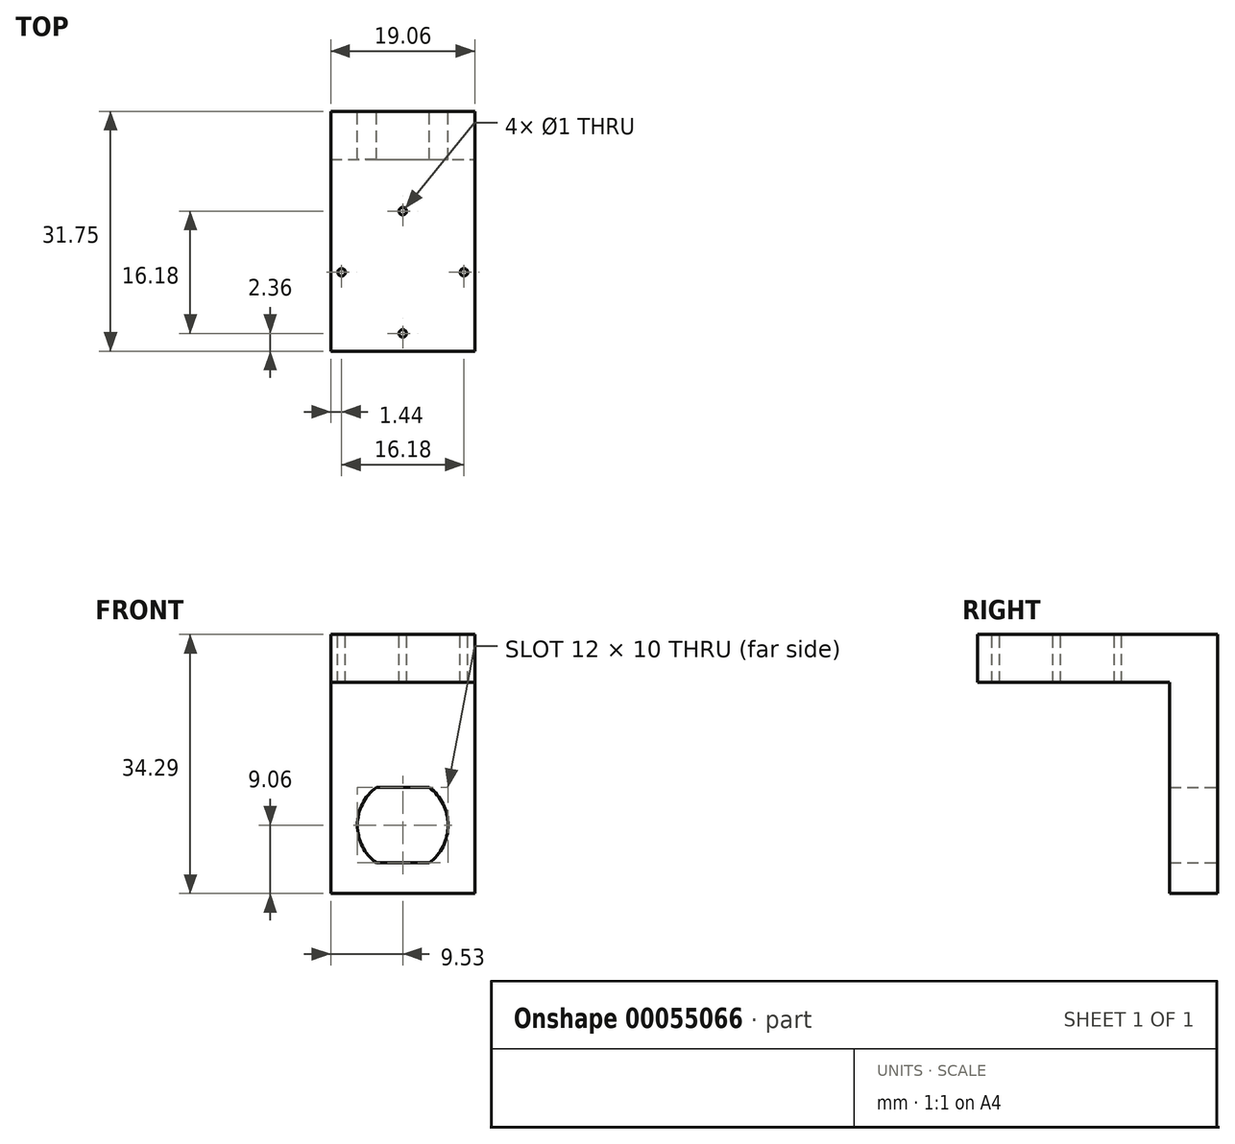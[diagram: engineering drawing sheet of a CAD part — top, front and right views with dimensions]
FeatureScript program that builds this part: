
annotation { "Feature Type Name" : "Feature", "Feature Type Description" : "" }
export const myFeature = defineFeature(function(context is Context, id is Id, definition is map)
    precondition{}
    {
        {
            var Q0;
            Q0=qCreatedBy(makeId("Front.planeOp"),FACE);
            var sketch = newSketch(context, id + "F0", { "sketchPlane" : qUnion([Q0])});
            skLineSegment(sketch, "E0.bottom", {"start": v(-9.52, -9.07) * mm, "end": v(9.52, -9.07) * mm});
            skLineSegment(sketch, "E0.top", {"start": v(-9.53, 25.23) * mm, "end": v(9.52, 25.23) * mm});
            skLineSegment(sketch, "E0.left", {"start": v(-9.53, -9.07) * mm, "end": v(-9.53, 25.23) * mm});
            skLineSegment(sketch, "E0.right", {"start": v(9.52, -9.07) * mm, "end": v(9.52, 25.23) * mm});
            skArc(sketch, "E1", {"start": v(-3.5, 5) * mm, "mid": v(-6, 0) * mm, "end": v(-3.5, -5) * mm});
            skArc(sketch, "E2", {"start": v(3.5, -5) * mm, "mid": v(6, 0) * mm, "end": v(3.5, 5) * mm});
            skLineSegment(sketch, "E3", {"start": v(-3.5, 5) * mm, "end": v(3.5, 5) * mm});
            skLineSegment(sketch, "E4", {"start": v(3.5, -5) * mm, "end": v(-3.5, -5) * mm});
            skLineSegment(sketch, "E5", {"start": v(-3.5, -5) * mm, "end": v(-6, -5) * mm, "construction": true});
            skLineSegment(sketch, "E6", {"start": v(-6, -5) * mm, "end": v(-6, 5) * mm, "construction": true});
            skLineSegment(sketch, "E7", {"start": v(-6, 5) * mm, "end": v(-3.5, 5) * mm, "construction": true});
            skLineSegment(sketch, "E8", {"start": v(3.5, 5) * mm, "end": v(6, 5) * mm, "construction": true});
            skLineSegment(sketch, "E9", {"start": v(6, 5) * mm, "end": v(6, -5) * mm, "construction": true});
            skLineSegment(sketch, "E10", {"start": v(6, -5) * mm, "end": v(3.5, -5) * mm, "construction": true});
            skPoint(sketch, "E11", {"position": v(0, 5) * mm});
            skPoint(sketch, "E12", {"position": v(0, -9.07) * mm});
            skCircle(sketch, "E13", {"center": v(0, 0) * mm, "radius": 10.8 * mm, "construction": true});
            skCircle(sketch, "E14", {"center": v(0, 0) * mm, "radius": 15.88 * mm, "construction": true});
            skPoint(sketch, "E15", {"position": v(0, 15.88) * mm});
            skLineSegment(sketch, "E16", {"start": v(-9.53, 18.88) * mm, "end": v(9.52, 18.88) * mm, "construction": true});
            skSolve(sketch);
        }
        {
            var Q0;
            Q0=qSketchRegion(id+"F0",true);
            extrude(context, id + "F1", {"entities" : qUnion([Q0]), "depth" : 6.35 * mm});
        }
        {
            var Q0;
            Q0=makeQuery(id+"F1.opExtrude","CAP_FACE",FACE,{"disambiguationData":[OSD([sQuery(id+"F0.wireOp",EDGE,"E0.bottom"),sQuery(id+"F0.wireOp",EDGE,"E0.top"),sQuery(id+"F0.wireOp",EDGE,"E0.left"),sQuery(id+"F0.wireOp",EDGE,"E0.right"),sQuery(id+"F0.wireOp",EDGE,"E1"),sQuery(id+"F0.wireOp",EDGE,"E2"),sQuery(id+"F0.wireOp",EDGE,"E3"),sQuery(id+"F0.wireOp",EDGE,"E4")])],"isStart":false});
            var sketch = newSketch(context, id + "F2", { "sketchPlane" : qUnion([Q0])});
            skLineSegment(sketch, "E17.bottom", {"start": v(-9.52, 25.23) * mm, "end": v(9.52, 25.23) * mm});
            skLineSegment(sketch, "E17.top", {"start": v(-9.53, 18.88) * mm, "end": v(9.52, 18.88) * mm});
            skLineSegment(sketch, "E17.left", {"start": v(-9.53, 25.23) * mm, "end": v(-9.53, 18.88) * mm});
            skLineSegment(sketch, "E17.right", {"start": v(9.52, 25.23) * mm, "end": v(9.52, 18.88) * mm});
            skSolve(sketch);
        }
        {
            var Q0;
            Q0=qSketchRegion(id+"F2",true);
            extrude(context, id + "F3", {"entities" : qUnion([Q0]), "operationType" : NewBodyOperationType.ADD, "depth" : 25.4 * mm});
        }
        {
            var Q0;
            Q0=makeQuery(id+"F3.boolean.opBoolean","MERGE",FACE,{"derivedFrom":[makeQuery(id+"F1.opExtrude","SWEPT_FACE",FACE,{"disambiguationData":[OSD([sQuery(id+"F0.wireOp",EDGE,"E0.top")])]}),makeQuery(id+"F3.opExtrude","SWEPT_FACE",FACE,{"disambiguationData":[OSD([sQuery(id+"F2.wireOp",EDGE,"E17.bottom")])]})]});
            var sketch = newSketch(context, id + "F4", { "sketchPlane" : qUnion([Q0])});
            skLineSegment(sketch, "E18", {"start": v(-9.53, -21.3) * mm, "end": v(9.53, -21.3) * mm, "construction": true});
            skPoint(sketch, "E19", {"position": v(0, -21.3) * mm});
            skCircle(sketch, "E20", {"center": v(-8.09, -21.3) * mm, "radius": 0.5 * mm});
            skCircle(sketch, "E21.1.0", {"center": v(0, -29.4) * mm, "radius": 0.5 * mm});
            skCircle(sketch, "E21.2.0", {"center": v(8.09, -21.3) * mm, "radius": 0.5 * mm});
            skCircle(sketch, "E21.3.0", {"center": v(0, -13.21) * mm, "radius": 0.5 * mm});
            skSolve(sketch);
        }
        {
            var Q0;
            Q0 = qSketchRegion(id + "F4", true);
            extrude(context, id + "F5", {"entities" : qUnion([Q0]), "operationType" : NewBodyOperationType.REMOVE, "endBound" : BoundingType.UP_TO_NEXT, "oppositeDirection" : true, "depth" : 25.4 * mm});
        }
    });
